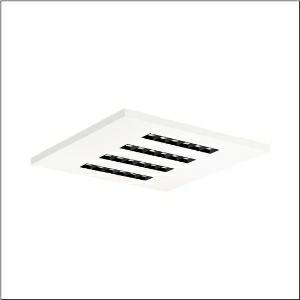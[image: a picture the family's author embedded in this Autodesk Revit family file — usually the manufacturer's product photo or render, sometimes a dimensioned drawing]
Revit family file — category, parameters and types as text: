
# Revit family: silica_21_square_51mx6kdu44w
name_source: partatom
category: Lighting Fixtures
units: mm (PartAtom-declared; Revit-internal decimal feet)

## family parameters
Cut with Voids When Loaded = No
Host = Face
Light Source = No
Part Type = Normal
Room Calculation Point = No
Round Connector Dimension = Use Diameter
Shared = No

## types (1)
- --- (1 x LED, 4600 lm, 29.6 W, 4000K)
    Apparent Load = 30 VA
    CIE Flux Codes = 86 100 100 100 100
    Color Rendering = 80
    Color Temperature = 4000K
    Default Elevation = 1800 mm
    Description = Silica 21 Square, office luminaire, primary light control with lens, of PMMA, primary anti-glare with reflector, of PC, black, CAT 2 (L<= 3000cd/m²), light emission: direct distribution, primary light characteristic: symmetric, installation type: lay-in mounting, LED, rated luminous flux: 4.600lm, luminous efficacy: 155lm/W, light colour: 840, colour temperature: 4000K, control gear: DALI 2, with terminal, 5-pole, mains connection: 220..240V, AC, 50/60Hz, rated input power: 29.6W, luminaire housing, of sheet steel, coated, traffic white (RAL 9016), module: M625, length: 622mm, width: 622mm, height: 33mm, protection rating (complete): IP20, insulation class (complete): insulation class I (protective earthing), certification: CE, ENEC, VDE, permissible operating ambient temperature: -20..+40°C, standard: EN 50419, packaging unit: 1 piece
    Height = 0 mm  [stored 0 ft]
    Lamp = 1 x LED
    Lamp Light Flux = 4600 lm
    Lamp Power = 29.6 W
    Lamp count = 1
    Length = 622 mm
    Luminous efficacy = 155 lm/W
    Manufacturer = Siteco
    ModVariant = No
    Model = 51MX6KDU44W
    Mounting Place = Ceiling
    Mounting Type = Recessed
    Number of Poles = 1
    OnlyDefault = Yes
    Power Factor = 1
    Product Name = Silica 21 Square
    Product group = office luminaire | ceiling recessed
    ProductGroupID = 400
    Protection Class = Protection class I
    Protection Degree = IP 20
    RLX_Detail_Level = 1
    RLX_Emergency_Light_Flux = 0 lm
    RLX_Emergency_Type = 0
    RLX_Emergency_Type_DB = No
    RlxData = <blob elided: 21181 chars, md5=c5a87bfb>
    Socket = socket
    Standby Power = 0 W
    System Light Flux = 4600 lm
    System Power = 30 W
    Type Comments = factory setting: luminous flux: 100 % | dim-lin: 254 | 399 mA
    Type Image = l_1275207.jpg
    URL = http://relux.com
    VarID = @adj_088995
    Voltage = 0 V
    Weight = 0.00 kg
    Width = 622 mm

note: [stored X ft] marks values corroborated as IEEE doubles in the binary element streams (Revit-internal decimal feet)

## geometry (parser evidence)
native form markers: Blend x4, Sweep x9
no freeform markers — native parametric forms only
